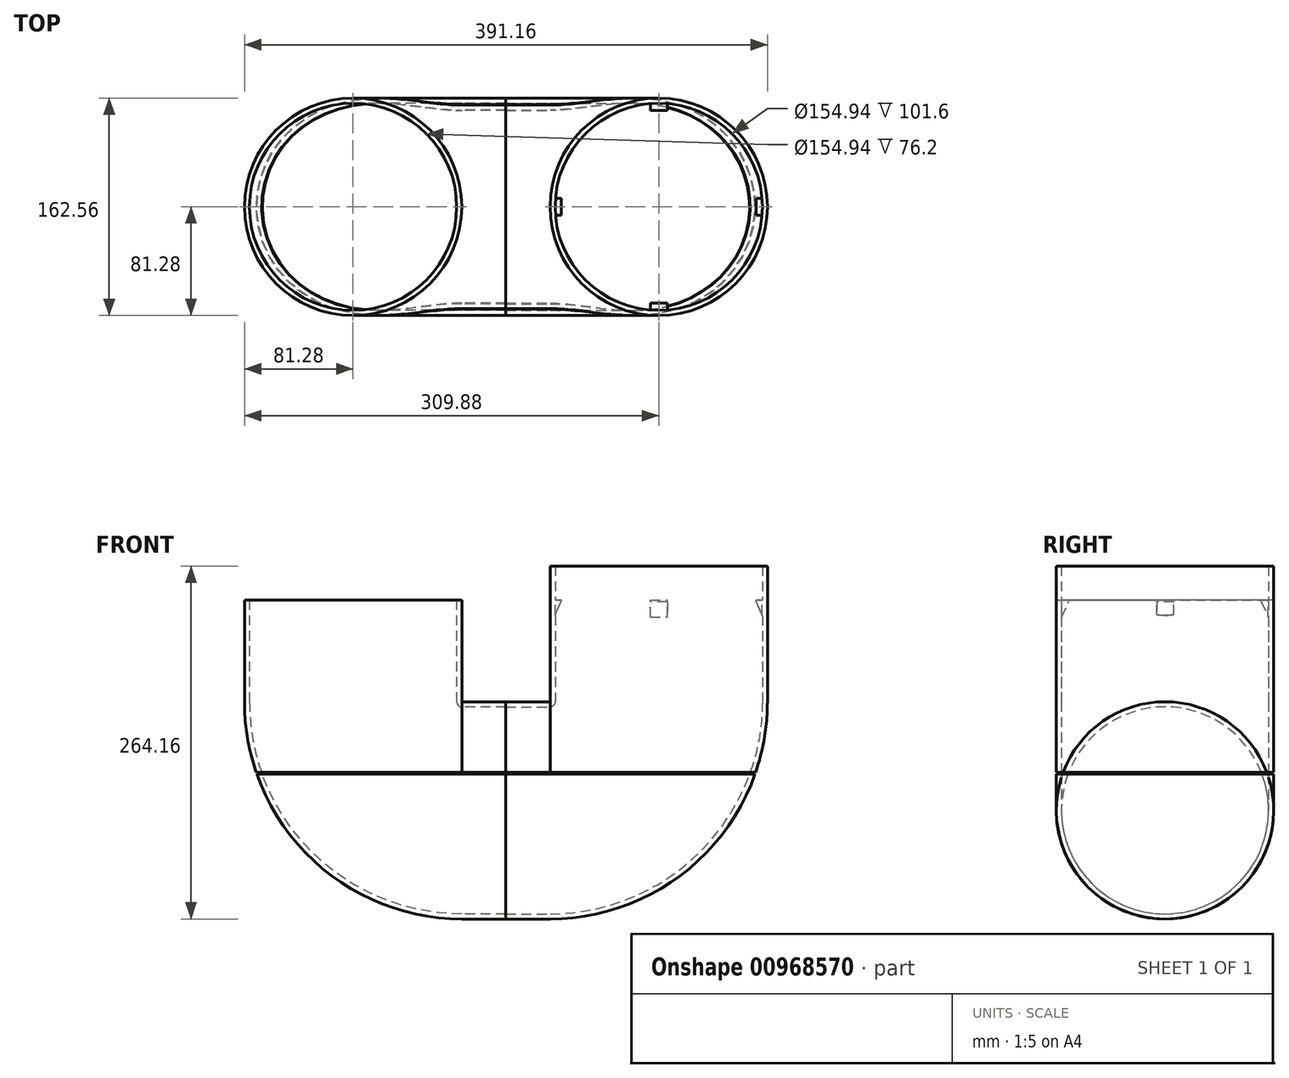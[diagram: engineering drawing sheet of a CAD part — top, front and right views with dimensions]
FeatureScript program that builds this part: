
annotation { "Feature Type Name" : "Feature", "Feature Type Description" : "" }
export const myFeature = defineFeature(function(context is Context, id is Id, definition is map)
    precondition{}
    {
        {
            var Q0;
            Q0=qCreatedBy(makeId("Top.planeOp"),FACE);
            var sketch = newSketch(context, id + "F0", { "sketchPlane" : qUnion([Q0])});
            skCircle(sketch, "E0", {"center": v(-114.3, 0) * mm, "radius": 77.47 * mm});
            skCircle(sketch, "E1", {"center": v(-114.3, 0) * mm, "radius": 81.28 * mm});
            skPoint(sketch, "E2", {"position": v(-33.02, 0) * mm});
            skPoint(sketch, "E3", {"position": v(-36.83, 0) * mm});
            skLineSegment(sketch, "E4.bottom", {"start": v(34.3, 5.03) * mm, "end": v(44.45, 5.03) * mm});
            skLineSegment(sketch, "E4.top", {"start": v(34.3, -5.13) * mm, "end": v(44.45, -5.13) * mm});
            skLineSegment(sketch, "E4.left", {"start": v(34.3, 5.03) * mm, "end": v(34.3, -5.13) * mm});
            skLineSegment(sketch, "E4.right", {"start": v(44.45, 5.03) * mm, "end": v(44.45, -5.13) * mm});
            skSolve(sketch);
        }
        {
            var Q0;
            Q0=makeQuery(id+"F0.imprint","IMPRINT",FACE,{"disambiguationData":[TD([[makeQuery(id+"F0.imprint","IMPRINT",EDGE,{"derivedFrom":sQuery(id+"F0.wireOp",EDGE,"E0")}),-1.0]])]});
            extrude(context, id + "F1", {"entities" : qUnion([Q0]), "depth" : 76.2 * mm, "offsetDistance" : 25.4 * mm});
        }
        {
            var Q0;
            Q0=qCreatedBy(makeId("Front.planeOp"),FACE);
            var sketch = newSketch(context, id + "F2", { "sketchPlane" : qUnion([Q0])});
            skPoint(sketch, "E5", {"position": v(-111.13, 0) * mm});
            skPoint(sketch, "E6", {"position": v(0, 0) * mm});
            skPoint(sketch, "E7.MirrorP", {"position": v(111.13, 0) * mm});
            skPoint(sketch, "E8", {"position": v(-33.02, 0) * mm});
            skLineSegment(sketch, "E9", {"start": v(-33.02, 100.02) * mm, "end": v(-33.02, -158.2) * mm, "construction": true});
            skArc(sketch, "E10", {"start": v(-111.13, 0) * mm, "mid": v(-88.25, -55.23) * mm, "end": v(-33.02, -78.1) * mm});
            skArc(sketch, "E11.MirrorCS", {"start": v(111.13, 0) * mm, "mid": v(88.25, -55.23) * mm, "end": v(33.02, -78.1) * mm});
            skLineSegment(sketch, "E12", {"start": v(-33.02, -78.1) * mm, "end": v(33.02, -78.1) * mm});
            skSolve(sketch);
        }
        {
            var Q0;
            Q0=makeQuery(id+"F1.opExtrude","CAP_FACE",FACE,{"disambiguationData":[OSD([sQuery(id+"F0.wireOp",EDGE,"E0"),sQuery(id+"F0.wireOp",EDGE,"E1")])],"isStart":true});
            var Q1;
            Q1=sQuery(id+"F2.wireOp",EDGE,"E10");
            revolve(context, id + "F3", {"operationType" : NewBodyOperationType.ADD, "surfaceOperationType" : NewSurfaceOperationType.NEW, "entities" : qUnion([Q0]), "axis" : qUnion([Q1]), "revolveType" : RevolveType.ONE_DIRECTION, "angle" : 90 * degree});
        }
        {
            var Q0;
            Q0=makeQuery(id+"F3.opRevolve","CAP_FACE",FACE,{"disambiguationData":[OSD([sQuery(id+"F0.wireOp",EDGE,"E0"),sQuery(id+"F0.wireOp",EDGE,"E1")])],"isStart":false});
            extrude(context, id + "F4", {"entities" : qUnion([Q0]), "operationType" : NewBodyOperationType.ADD, "depth" : 33.02 * mm, "offsetDistance" : 25.4 * mm});
        }
        {
            var Q0;
            Q0=qCreatedBy(makeId("Top.planeOp"),FACE);
            cPlane(context, id + "F5", {"entities" : qUnion([Q0]), "cplaneType" : CPlaneType.OFFSET, "offset" : 52.83 * mm, "oppositeDirection" : true, "width" : 152.4 * mm, "height" : 152.4 * mm});
        }
        {
            var Q0;
            Q0=qCreatedBy(id+"F5.planeOp",FACE);
            var sketch = newSketch(context, id + "F6", { "sketchPlane" : qUnion([Q0])});
            skLineSegment(sketch, "E13.bottom", {"start": v(114.57, 104.91) * mm, "end": v(-197.16, 104.91) * mm});
            skLineSegment(sketch, "E13.top", {"start": v(114.57, -91.16) * mm, "end": v(-197.16, -91.16) * mm});
            skLineSegment(sketch, "E13.left", {"start": v(114.57, 104.91) * mm, "end": v(114.57, -91.16) * mm});
            skLineSegment(sketch, "E13.right", {"start": v(-197.16, 104.91) * mm, "end": v(-197.16, -91.16) * mm});
            skSolve(sketch);
        }
        {
            var Q0;
            Q0=makeQuery(id+"F6.imprint","IMPRINT",FACE,{"disambiguationData":[TD([[makeQuery(id+"F6.imprint","IMPRINT",EDGE,{"derivedFrom":sQuery(id+"F6.wireOp",EDGE,"E13.bottom")}),1.0]])]});
            extrude(context, id + "F7", {"entities" : qUnion([Q0]), "operationType" : NewBodyOperationType.REMOVE, "oppositeDirection" : true, "depth" : 1.27 * mm, "offsetDistance" : 25.4 * mm});
        }
        {
            var Q0;
            Q0=makeQuery(id+"F1.opExtrude","SWEPT_BODY",BODY,{"disambiguationData":[OSD([sQuery(id+"F0.wireOp",EDGE,"E0"),sQuery(id+"F0.wireOp",EDGE,"E1")])]});
            var Q1;
            Q1=qCreatedBy(makeId("Right.planeOp"),FACE);
            mirror(context, id + "F8", {"entities" : qUnion([Q0]), "mirrorPlane" : qUnion([Q1])});
        }
        {
            var Q0;
            Q0=makeQuery(id+"F8.opPattern","COPY",FACE,{"derivedFrom":makeQuery(id+"F1.opExtrude","CAP_FACE",FACE,{"disambiguationData":[OSD([sQuery(id+"F0.wireOp",EDGE,"E0"),sQuery(id+"F0.wireOp",EDGE,"E1")])],"isStart":false}),"instanceName":"1"});
            var sketch = newSketch(context, id + "F9", { "sketchPlane" : qUnion([Q0])});
            skLineSegment(sketch, "E14", {"start": v(37.1, 6.53) * mm, "end": v(41.5, 6.53) * mm});
            skLineSegment(sketch, "E15", {"start": v(41.5, 6.53) * mm, "end": v(41.5, -6.17) * mm});
            skLineSegment(sketch, "E16", {"start": v(41.5, -6.17) * mm, "end": v(37.08, -6.17) * mm});
            skPoint(sketch, "E17", {"position": v(114.3, 0) * mm});
            skPoint(sketch, "E18", {"position": v(114.3, 110.05) * mm});
            skPoint(sketch, "E19", {"position": v(114.3, -93.97) * mm});
            skLineSegment(sketch, "E20", {"start": v(114.3, 110.05) * mm, "end": v(114.3, -93.97) * mm, "construction": true});
            skLineSegment(sketch, "E21.MirrorCS", {"start": v(191.5, 6.53) * mm, "end": v(187.1, 6.53) * mm});
            skLineSegment(sketch, "E22.MirrorCS", {"start": v(187.1, 6.53) * mm, "end": v(187.1, -6.17) * mm});
            skLineSegment(sketch, "E23.MirrorCS", {"start": v(187.1, -6.17) * mm, "end": v(191.52, -6.17) * mm});
            skLineSegment(sketch, "E24", {"start": v(107.95, -77.2) * mm, "end": v(107.95, -72.13) * mm});
            skLineSegment(sketch, "E25", {"start": v(107.95, -72.13) * mm, "end": v(120.65, -72.13) * mm});
            skLineSegment(sketch, "E26", {"start": v(120.65, -72.13) * mm, "end": v(120.65, -77.2) * mm});
            skLineSegment(sketch, "E27", {"start": v(0, 0) * mm, "end": v(283.54, 0) * mm, "construction": true});
            skLineSegment(sketch, "E28.MirrorCS", {"start": v(107.95, 72.13) * mm, "end": v(120.65, 72.13) * mm});
            skLineSegment(sketch, "E29.MirrorCS", {"start": v(120.65, 72.13) * mm, "end": v(120.65, 77.2) * mm});
            skLineSegment(sketch, "E30.MirrorCS", {"start": v(107.95, 77.2) * mm, "end": v(107.95, 72.13) * mm});
            skSolve(sketch);
        }
        {
            var Q0;
            Q0=makeQuery(id+"F9.imprint","IMPRINT",FACE,{"disambiguationData":[TD([[makeQuery(id+"F9.imprint","IMPRINT",EDGE,{"derivedFrom":sQuery(id+"F9.wireOp",EDGE,"E28.MirrorCS")}),1.0]])]});
            var Q1;
            {var subQ0=sQuery(id+"F9.wireOp",EDGE,"E21.MirrorCS");Q1=makeQuery(id+"F9.imprint","IMPRINT",FACE,{"disambiguationData":[TD([[makeQuery(id+"F9.imprint","IMPRINT",EDGE,{"derivedFrom":subQ0}),1.0]])]});}
            var Q2;
            {var subQ0=sQuery(id+"F9.wireOp",EDGE,"E24");Q2=makeQuery(id+"F9.imprint","IMPRINT",FACE,{"disambiguationData":[TD([[makeQuery(id+"F9.imprint","IMPRINT",EDGE,{"derivedFrom":subQ0}),-1.0]])]});}
            var Q3;
            {var subQ0=sQuery(id+"F9.wireOp",EDGE,"E14");Q3=makeQuery(id+"F9.imprint","IMPRINT",FACE,{"disambiguationData":[TD([[makeQuery(id+"F9.imprint","IMPRINT",EDGE,{"derivedFrom":subQ0}),-1.0]])]});}
            extrude(context, id + "F10", {"entities" : qUnion([Q0, Q1, Q2, Q3]), "operationType" : NewBodyOperationType.ADD, "depth" : -12.7 * mm, "offsetDistance" : 25.4 * mm});
        }
        {
            var Q0;
            Q0=makeQuery(id+"F9.imprint","IMPRINT",FACE,{"disambiguationData":[TD([[makeQuery(id+"F9.imprint","IMPRINT",EDGE,{"derivedFrom":makeQuery(id+"F8.opPattern","COPY",EDGE,{"derivedFrom":makeQuery(id+"F1.opExtrude","CAP_EDGE",EDGE,{"disambiguationData":[OSD([sQuery(id+"F0.wireOp",EDGE,"E1")])],"isStart":false}),"instanceName":"1"})}),-1.0]])]});
            extrude(context, id + "F11", {"entities" : qUnion([Q0]), "operationType" : NewBodyOperationType.ADD, "depth" : 25.4 * mm, "offsetDistance" : 25.4 * mm});
        }
        {
            var Q0;
            Q0=makeQuery(id+"F10.opExtrude","CAP_EDGE",EDGE,{"disambiguationData":[OSD([sQuery(id+"F9.wireOp",EDGE,"E15")])],"isStart":false});
            chamfer(context, id + "F12", {"entities" : qUnion([Q0]), "chamferType" : ChamferType.OFFSET_ANGLE, "width" : 5.08 * mm, "oppositeDirection" : false, "angle" : 68 * degree, "tangentPropagation" : true});
        }
        {
            var Q0;
            Q0=makeQuery(id+"F10.opExtrude","CAP_EDGE",EDGE,{"disambiguationData":[OSD([sQuery(id+"F9.wireOp",EDGE,"E28.MirrorCS")])],"isStart":false});
            var Q1;
            Q1=makeQuery(id+"F10.opExtrude","CAP_EDGE",EDGE,{"disambiguationData":[OSD([sQuery(id+"F9.wireOp",EDGE,"E22.MirrorCS")])],"isStart":false});
            chamfer(context, id + "F13", {"entities" : qUnion([Q0, Q1]), "chamferType" : ChamferType.TWO_OFFSETS, "width1" : 11.43 * mm, "oppositeDirection" : false, "width2" : 5.08 * mm, "tangentPropagation" : true});
        }
        {
            var Q0;
            Q0=makeQuery(id+"F10.opExtrude","CAP_EDGE",EDGE,{"disambiguationData":[OSD([sQuery(id+"F9.wireOp",EDGE,"E25")])],"isStart":false});
            chamfer(context, id + "F14", {"entities" : qUnion([Q0]), "chamferType" : ChamferType.TWO_OFFSETS, "width1" : 5.08 * mm, "oppositeDirection" : false, "width2" : 11.43 * mm, "tangentPropagation" : true});
        }
    });
